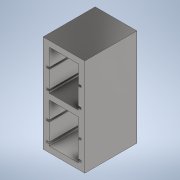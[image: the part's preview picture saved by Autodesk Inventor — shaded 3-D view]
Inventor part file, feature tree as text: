
AUTODESK INVENTOR PART (.ipt)
format: ipt  version: 2021 (Build 250183000, 183)  size: 169,472 bytes
history: native  units: in
note: dims shown in document units (in); Inventor stores cm internally (conversion verified against a paired STEP export)
features: extrude x1, sketch x1
ambient origin geometry x8: Origin, YZ Plane, XZ Plane, XY Plane, X Axis, Y Axis, Z Axis, Center Point
bodies: Body1 (feature_tree)
feature tree (2):
  extrude  "Extrusion5"  Depth=1.1811in
  sketch  "Sketch7"  dims[d75=0.1969in d86=1.1811in d87=0.1969in d88=0.1181in d90=1.1811in d91=0.1969in d92=0.1181in d93=0.1181in d94=1.9685in d95=1.9685in d96=3.5433in d97=0.0in d98=3.3465in d99=2.8346in d100=2.7165in d101=1.9685in d103=1.1811in d104=0.1969in d105=0.1181in d106=1.1811in d107=0.1969in d108=0.1181in d109=0.1816in d110=0.3937in d111=0.3937in d112=0.3937in d113=0.1181in d114=0.0344in d115=0.0197in d116=0.0344in]
